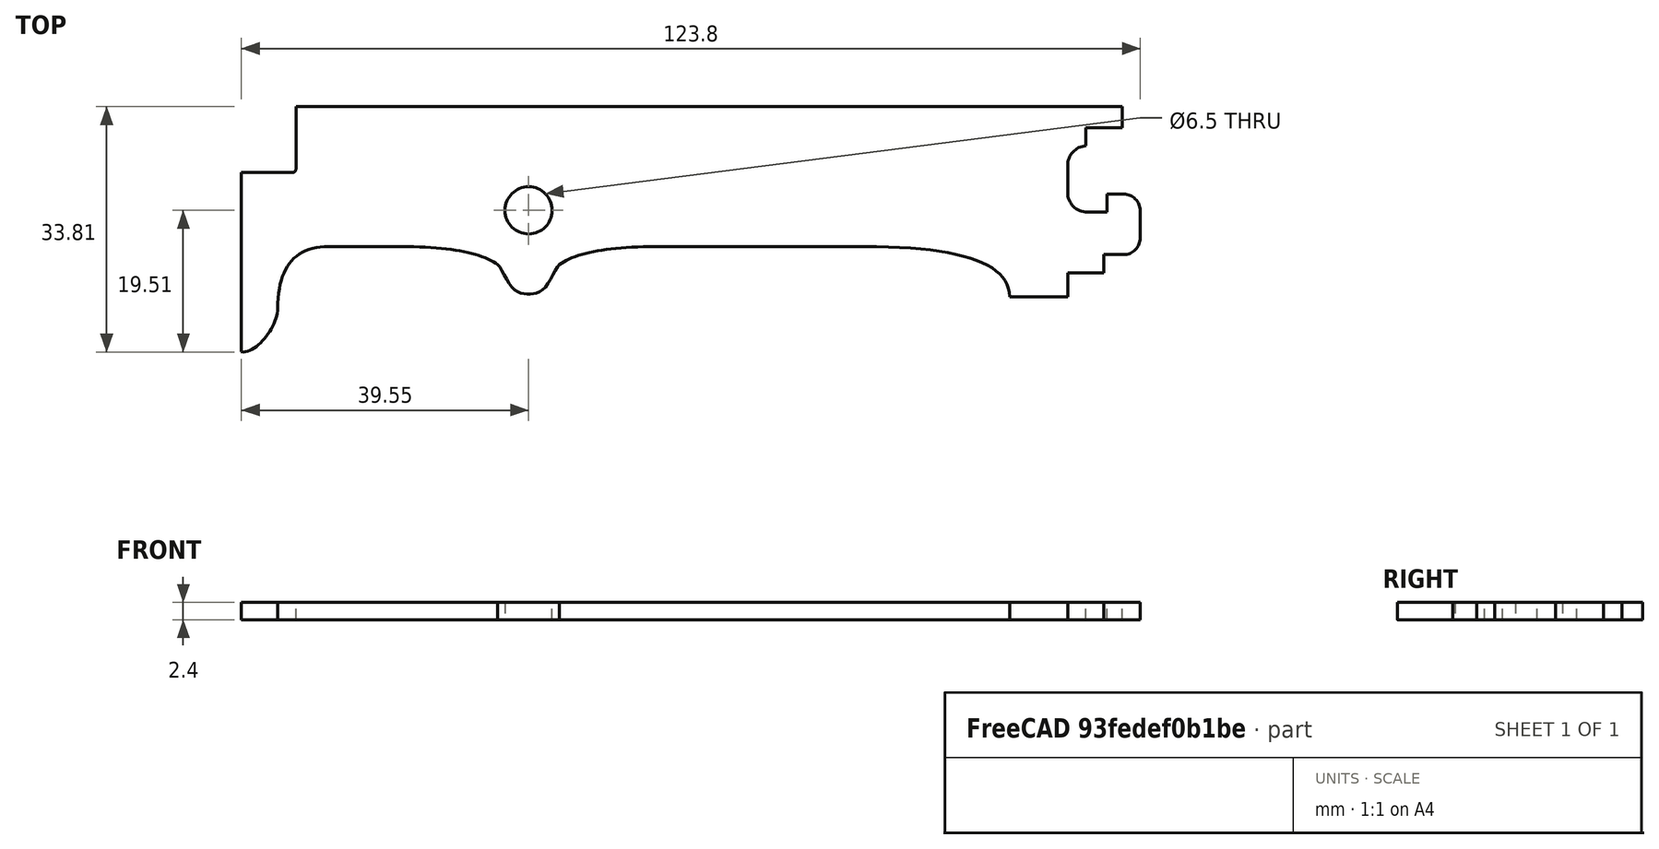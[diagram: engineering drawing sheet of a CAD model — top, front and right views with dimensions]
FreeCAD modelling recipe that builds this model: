
FCSTD DOCUMENT  (FreeCAD 0.19R0.19.2)
Label: v0_11
License: All rights reserved
LicenseURL: http://en.wikipedia.org/wiki/All_rights_reserved
objects: Sketcher::SketchObject×2, Part::Extrusion×1
note: 3 computed .brp shape members not serialized (recipe doc carries the construction recipe); baked Part::Feature solids carry a one-line shape summary decoded from their .brp

FEATURE [Sketcher::SketchObject] Sketch
  FullyConstrained = true
  sketch-geometry (69):
    g0: ArcOfCircle CenterX=-20 CenterY=-14.35 CenterZ=0 NormalX=0 NormalY=0 NormalZ=1 AngleXU=0 Radius=2.3 StartAngle=8e-16 EndAngle=1.5708
    g1: ArcOfCircle CenterX=-20 CenterY=-18.1 CenterZ=0 NormalX=0 NormalY=0 NormalZ=1 AngleXU=0 Radius=2.3 StartAngle=4.71239 EndAngle=6.28319
    g2: LineSegment StartX=-20 StartY=-20.4 StartZ=0 EndX=-22.7 EndY=-20.4 EndZ=0
    g3: LineSegment StartX=-22.7 StartY=-22.9 StartZ=0 EndX=-22.7 EndY=-20.4 EndZ=0
    g4: LineSegment StartX=-17.7 StartY=-14.35 StartZ=0 EndX=-17.7 EndY=-18.1 EndZ=0
    g5: LineSegment StartX=-25.2 StartY=-5.40742 StartZ=0 EndX=-25.2 EndY=-2.9 EndZ=0
    g6: LineSegment StartX=-25.2 StartY=-2.9 StartZ=0 EndX=-20.2 EndY=-2.9 EndZ=0
    g7: LineSegment StartX=-20.2 StartY=-2.9 StartZ=0 EndX=-20.2 EndY=0 EndZ=0
    g8: ArcOfCircle CenterX=-25 CenterY=-8.1 CenterZ=0 NormalX=0 NormalY=0 NormalZ=1 AngleXU=0 Radius=2.7 StartAngle=1.64494 EndAngle=3.14159
    g9: ArcOfCircle CenterX=-25 CenterY=-11.85 CenterZ=0 NormalX=0 NormalY=0 NormalZ=1 AngleXU=0 Radius=2.7 StartAngle=3.14159 EndAngle=4.71239
    g10: LineSegment StartX=-27.7 StartY=-8.1 StartZ=0 EndX=-27.7 EndY=-11.85 EndZ=0
    g11: LineSegment StartX=-25 StartY=-14.55 StartZ=0 EndX=-22.3 EndY=-14.55 EndZ=0
    g12: LineSegment StartX=-22.3 StartY=-12.05 StartZ=0 EndX=-22.3 EndY=-14.55 EndZ=0
    g13: LineSegment StartX=-22.3 StartY=-12.05 StartZ=0 EndX=-20 EndY=-12.05 EndZ=0
    g14: LineSegment StartX=-27.7 StartY=-22.9 StartZ=0 EndX=-22.7 EndY=-22.9 EndZ=0
    g15: LineSegment StartX=-27.7 StartY=-22.9 StartZ=0 EndX=-27.7 EndY=-26.2 EndZ=0
    g16: Circle CenterX=-101.95 CenterY=-14.3 CenterZ=0 NormalX=0 NormalY=0 NormalZ=1 AngleXU=0 Radius=3.25
    g17: LineSegment StartX=-134 StartY=0 StartZ=0 EndX=-20.2 EndY=0 EndZ=0
    g18: LineSegment StartX=-134 StartY=2.68e-14 StartZ=0 EndX=-134 EndY=-8.6 EndZ=0
    g19: LineSegment StartX=-134.5 StartY=-9.1 StartZ=0 EndX=-141.5 EndY=-9.1 EndZ=0
    g20: ArcOfCircle CenterX=-134.5 CenterY=-8.6 CenterZ=0 NormalX=0 NormalY=0 NormalZ=1 AngleXU=0 Radius=0.5 StartAngle=4.71239 EndAngle=6.28319
    g21: Circle CenterX=-97.7 CenterY=-21.8 CenterZ=0 NormalX=0 NormalY=0 NormalZ=1 AngleXU=0 Radius=1
    g22: Circle CenterX=-94.45 CenterY=-19.3 CenterZ=0 NormalX=0 NormalY=0 NormalZ=1 AngleXU=0 Radius=1
    g23: Circle CenterX=-84.45 CenterY=-19.3 CenterZ=0 NormalX=0 NormalY=0 NormalZ=1 AngleXU=0 Radius=1
    g24: BSplineCurve PolesCount=3 KnotsCount=2 Degree=2 IsPeriodic=0
    g25: GeomPoint X=-97.7 Y=-21.8 Z=0
    g26: GeomPoint X=-84.45 Y=-19.3 Z=0
    g27: Circle CenterX=-106.2 CenterY=-21.8 CenterZ=0 NormalX=0 NormalY=0 NormalZ=1 AngleXU=0 Radius=1
    g28: Circle CenterX=-109.45 CenterY=-19.3 CenterZ=0 NormalX=0 NormalY=0 NormalZ=1 AngleXU=0 Radius=1
    g29: Circle CenterX=-119.45 CenterY=-19.3 CenterZ=0 NormalX=0 NormalY=0 NormalZ=1 AngleXU=0 Radius=1
    g30: BSplineCurve PolesCount=3 KnotsCount=2 Degree=2 IsPeriodic=0
    g31: GeomPoint X=-106.2 Y=-21.8 Z=0
    g32: GeomPoint X=-119.45 Y=-19.3 Z=0
    g33: LineSegment StartX=-141.5 StartY=-9.1 StartZ=0 EndX=-141.5 EndY=-33.8 EndZ=0
    g34-g37: Circle x4 (B-spline internal-alignment scaffolding for g38; pole/knot coordinates omitted)
    g38: BSplineCurve PolesCount=4 KnotsCount=2 Degree=3 IsPeriodic=0
    g39: GeomPoint X=-141.5 Y=-33.8 Z=0
    g40: GeomPoint X=-136.5 Y=-27.8 Z=0
    g41: Circle CenterX=-136.5 CenterY=-27.8 CenterZ=0 NormalX=0 NormalY=0 NormalZ=1 AngleXU=0 Radius=1
    g42: Circle CenterX=-136.5 CenterY=-19.3 CenterZ=0 NormalX=0 NormalY=0 NormalZ=1 AngleXU=0 Radius=1
    g43: Circle CenterX=-129.5 CenterY=-19.3 CenterZ=0 NormalX=0 NormalY=0 NormalZ=1 AngleXU=0 Radius=1
    g44: BSplineCurve PolesCount=3 KnotsCount=2 Degree=2 IsPeriodic=0
    g45: GeomPoint X=-136.5 Y=-27.8 Z=0
    g46: GeomPoint X=-129.5 Y=-19.3 Z=0
    g47: LineSegment StartX=-129.5 StartY=-19.3 StartZ=0 EndX=-119.45 EndY=-19.3 EndZ=0
    g48: LineSegment StartX=-35.7 StartY=-26.2 StartZ=0 EndX=-27.7 EndY=-26.2 EndZ=0
    g49: Circle CenterX=-35.7 CenterY=-26.2 CenterZ=0 NormalX=0 NormalY=0 NormalZ=1 AngleXU=0 Radius=1
    g50: Circle CenterX=-35.7 CenterY=-19.3 CenterZ=0 NormalX=0 NormalY=0 NormalZ=1 AngleXU=0 Radius=1
    g51: Circle CenterX=-55.7 CenterY=-19.3 CenterZ=0 NormalX=0 NormalY=0 NormalZ=1 AngleXU=0 Radius=1
    g52: BSplineCurve PolesCount=3 KnotsCount=2 Degree=2 IsPeriodic=0
    g53: GeomPoint X=-35.7 Y=-26.2 Z=0
    g54: GeomPoint X=-55.7 Y=-19.3 Z=0
    g55: LineSegment StartX=-84.45 StartY=-19.3 StartZ=0 EndX=-55.7 EndY=-19.3 EndZ=0
    g56-g62: Circle x7 (B-spline internal-alignment scaffolding for g63; pole/knot coordinates omitted)
    g63: BSplineCurve PolesCount=7 KnotsCount=5 Degree=3 IsPeriodic=0
    g64-g68: GeomPoint x5 (B-spline internal-alignment scaffolding for g63; pole/knot coordinates omitted)
  constraints (111):
    c: Block(g1)
    c: Block(g0)
    c: Coincident(g2,g1)
    c: Horizontal(g2)
    c: Vertical(g3)
    c: Coincident(g3,g2)
    c: Coincident(g4,g0)
    c: Coincident(g4,g1)
    c: Vertical(g4)
    c: Vertical(g5)
    c: Block(g5)
    c: Coincident(g6,g5)
    c: Horizontal(g6)
    c: Vertical(g7)
    c: Block(g7)
    c: Block(g6)
    c: Coincident(g8,g5)
    c: Block(g9)
    c: Coincident(g10,g8)
    c: Coincident(g10,g9)
    c: Vertical(g10)
    c: Block(g10)
    c: Coincident(g11,g9)
    c: Horizontal(g11)
    c: Vertical(g12)
    c: Coincident(g12,g11)
    c: Block(g12)
    c: Coincident(g13,g0)
    c: Horizontal(g13)
    c: Block(g13)
    c: Coincident(g14,g3)
    c: Horizontal(g14)
    c: Block(g14)
    c: Coincident(g15,g14)
    c: Vertical(g15)
    c: Block(g16)
    c: Coincident(g17,g7)
    c: Horizontal(g17)
    c: Vertical(g18)
    c: Distance(g18) = 8.6
    c: Horizontal(g19)
    c: Distance(g19) = 7
    c: Coincident(g20,g18)
    c: Coincident(g20,g19)
    c: Block(g20)
    c: Block(g17)
    c: Weight(g21) = 1
    c: Equal(g21,g22)
    c: Equal(g21,g23)
    c: InternalAlignment(g21,g24)
    c: InternalAlignment(g22,g24)
    c: InternalAlignment(g23,g24)
    c: InternalAlignment(g25,g24)
    c: InternalAlignment(g26,g24)
    c: Weight(g27) = 1
    c: Equal(g27,g28)
    c: Equal(g27,g29)
    c: InternalAlignment(g27,g30)
    c: InternalAlignment(g28,g30)
    c: InternalAlignment(g29,g30)
    c: InternalAlignment(g31,g30)
    c: InternalAlignment(g32,g30)
    c: Block(g30)
    c: Block(g24)
    c: Coincident(g33,g19)
    c: Vertical(g33)
    c: Block(g33)
    c: Coincident(g38,g33)
    c: Weight(g34) = 1
    c: Equal(g34,g35)
    c: Equal(g34,g36)
    c: Equal(g34,g37)
    c: InternalAlignment(g34-g37 -> g38) x4
    c: InternalAlignment(g39,g38)
    c: InternalAlignment(g40,g38)
    c: Weight(g41) = 1
    c: Equal(g41,g42)
    c: Equal(g41,g43)
    c: InternalAlignment(g41,g44)
    c: InternalAlignment(g42,g44)
    c: InternalAlignment(g43,g44)
    c: InternalAlignment(g45,g44)
    c: InternalAlignment(g46,g44)
    c: Block(g38)
    c: Block(g44)
    c: Coincident(g47,g44)
    c: Coincident(g47,g30)
    c: Horizontal(g47)
    c: Horizontal(g48)
    c: Distance(g48) = 8
    c: Block(g48)
    c: Block(g15)
    c: Block(g8)
    c: Coincident(g52,g48)
    c: Weight(g49) = 1
    c: Equal(g49,g50)
    c: Equal(g49,g51)
    c: InternalAlignment(g49,g52)
    c: InternalAlignment(g50,g52)
    c: InternalAlignment(g51,g52)
    c: InternalAlignment(g53,g52)
    c: InternalAlignment(g54,g52)
    c: Block(g52)
    c: Coincident(g55,g24)
    c: Coincident(g55,g52)
    c: Horizontal(g55)
    c: Weight(g56) = 1
    c: Equal(g56, g57-g62) x6
    c: InternalAlignment(g56-g62 -> g63) x7
    c: InternalAlignment(g64-g68 -> g63) x5
    c: Block(g63)
FEATURE [Part::Extrusion] Extrude
  Base = -> Sketch
  Dir = (0,0,1)
  DirMode = 2
  FaceMakerClass = Part::FaceMakerBullseye
  LengthFwd = 2.4
  LengthRev = 0
  Solid = true
  Symmetric = false
FEATURE [Sketcher::SketchObject] Sketch001
  FullyConstrained = true
  sketch-geometry (69):
    g0: ArcOfCircle CenterX=-20 CenterY=-14.35 CenterZ=0 NormalX=0 NormalY=0 NormalZ=1 AngleXU=0 Radius=2.3 StartAngle=8e-16 EndAngle=1.5708
    g1: ArcOfCircle CenterX=-20 CenterY=-18.1 CenterZ=0 NormalX=0 NormalY=0 NormalZ=1 AngleXU=0 Radius=2.3 StartAngle=4.71239 EndAngle=6.28319
    g2: LineSegment StartX=-20 StartY=-20.4 StartZ=0 EndX=-22.7 EndY=-20.4 EndZ=0
    g3: LineSegment StartX=-22.7 StartY=-22.9 StartZ=0 EndX=-22.7 EndY=-20.4 EndZ=0
    g4: LineSegment StartX=-17.7 StartY=-14.35 StartZ=0 EndX=-17.7 EndY=-18.1 EndZ=0
    g5: LineSegment StartX=-25.2 StartY=-5.40742 StartZ=0 EndX=-25.2 EndY=-2.9 EndZ=0
    g6: LineSegment StartX=-25.2 StartY=-2.9 StartZ=0 EndX=-20.2 EndY=-2.9 EndZ=0
    g7: LineSegment StartX=-20.2 StartY=-2.9 StartZ=0 EndX=-20.2 EndY=0 EndZ=0
    g8: ArcOfCircle CenterX=-25 CenterY=-8.1 CenterZ=0 NormalX=0 NormalY=0 NormalZ=1 AngleXU=0 Radius=2.7 StartAngle=1.64494 EndAngle=3.14159
    g9: ArcOfCircle CenterX=-25 CenterY=-11.85 CenterZ=0 NormalX=0 NormalY=0 NormalZ=1 AngleXU=0 Radius=2.7 StartAngle=3.14159 EndAngle=4.71239
    g10: LineSegment StartX=-27.7 StartY=-8.1 StartZ=0 EndX=-27.7 EndY=-11.85 EndZ=0
    g11: LineSegment StartX=-25 StartY=-14.55 StartZ=0 EndX=-22.3 EndY=-14.55 EndZ=0
    g12: LineSegment StartX=-22.3 StartY=-12.05 StartZ=0 EndX=-22.3 EndY=-14.55 EndZ=0
    g13: LineSegment StartX=-22.3 StartY=-12.05 StartZ=0 EndX=-20 EndY=-12.05 EndZ=0
    g14: LineSegment StartX=-27.7 StartY=-22.9 StartZ=0 EndX=-22.7 EndY=-22.9 EndZ=0
    g15: LineSegment StartX=-27.7 StartY=-22.9 StartZ=0 EndX=-27.7 EndY=-26.2 EndZ=0
    g16: Circle CenterX=-101.95 CenterY=-14.3 CenterZ=0 NormalX=0 NormalY=0 NormalZ=1 AngleXU=0 Radius=3.25
    g17: LineSegment StartX=-134 StartY=0 StartZ=0 EndX=-20.2 EndY=0 EndZ=0
    g18: LineSegment StartX=-134 StartY=2.68e-14 StartZ=0 EndX=-134 EndY=-8.6 EndZ=0
    g19: LineSegment StartX=-134.5 StartY=-9.1 StartZ=0 EndX=-141.5 EndY=-9.1 EndZ=0
    g20: ArcOfCircle CenterX=-134.5 CenterY=-8.6 CenterZ=0 NormalX=0 NormalY=0 NormalZ=1 AngleXU=0 Radius=0.5 StartAngle=4.71239 EndAngle=6.28319
    g21: Circle CenterX=-97.7 CenterY=-21.8 CenterZ=0 NormalX=0 NormalY=0 NormalZ=1 AngleXU=0 Radius=1
    g22: Circle CenterX=-94.45 CenterY=-19.3 CenterZ=0 NormalX=0 NormalY=0 NormalZ=1 AngleXU=0 Radius=1
    g23: Circle CenterX=-84.45 CenterY=-19.3 CenterZ=0 NormalX=0 NormalY=0 NormalZ=1 AngleXU=0 Radius=1
    g24: BSplineCurve PolesCount=3 KnotsCount=2 Degree=2 IsPeriodic=0
    g25: GeomPoint X=-97.7 Y=-21.8 Z=0
    g26: GeomPoint X=-84.45 Y=-19.3 Z=0
    g27: Circle CenterX=-106.2 CenterY=-21.8 CenterZ=0 NormalX=0 NormalY=0 NormalZ=1 AngleXU=0 Radius=1
    g28: Circle CenterX=-109.45 CenterY=-19.3 CenterZ=0 NormalX=0 NormalY=0 NormalZ=1 AngleXU=0 Radius=1
    g29: Circle CenterX=-119.45 CenterY=-19.3 CenterZ=0 NormalX=0 NormalY=0 NormalZ=1 AngleXU=0 Radius=1
    g30: BSplineCurve PolesCount=3 KnotsCount=2 Degree=2 IsPeriodic=0
    g31: GeomPoint X=-106.2 Y=-21.8 Z=0
    g32: GeomPoint X=-119.45 Y=-19.3 Z=0
    g33: LineSegment StartX=-141.5 StartY=-9.1 StartZ=0 EndX=-141.5 EndY=-33.8 EndZ=0
    g34-g37: Circle x4 (B-spline internal-alignment scaffolding for g38; pole/knot coordinates omitted)
    g38: BSplineCurve PolesCount=4 KnotsCount=2 Degree=3 IsPeriodic=0
    g39: GeomPoint X=-141.5 Y=-33.8 Z=0
    g40: GeomPoint X=-136.5 Y=-27.8 Z=0
    g41: Circle CenterX=-136.5 CenterY=-27.8 CenterZ=0 NormalX=0 NormalY=0 NormalZ=1 AngleXU=0 Radius=1
    g42: Circle CenterX=-136.5 CenterY=-19.3 CenterZ=0 NormalX=0 NormalY=0 NormalZ=1 AngleXU=0 Radius=1
    g43: Circle CenterX=-129.5 CenterY=-19.3 CenterZ=0 NormalX=0 NormalY=0 NormalZ=1 AngleXU=0 Radius=1
    g44: BSplineCurve PolesCount=3 KnotsCount=2 Degree=2 IsPeriodic=0
    g45: GeomPoint X=-136.5 Y=-27.8 Z=0
    g46: GeomPoint X=-129.5 Y=-19.3 Z=0
    g47: LineSegment StartX=-129.5 StartY=-19.3 StartZ=0 EndX=-119.45 EndY=-19.3 EndZ=0
    g48: LineSegment StartX=-35.7 StartY=-26.2 StartZ=0 EndX=-27.7 EndY=-26.2 EndZ=0
    g49: Circle CenterX=-35.7 CenterY=-26.2 CenterZ=0 NormalX=0 NormalY=0 NormalZ=1 AngleXU=0 Radius=1
    g50: Circle CenterX=-35.7 CenterY=-19.3 CenterZ=0 NormalX=0 NormalY=0 NormalZ=1 AngleXU=0 Radius=1
    g51: Circle CenterX=-55.7 CenterY=-19.3 CenterZ=0 NormalX=0 NormalY=0 NormalZ=1 AngleXU=0 Radius=1
    g52: BSplineCurve PolesCount=3 KnotsCount=2 Degree=2 IsPeriodic=0
    g53: GeomPoint X=-35.7 Y=-26.2 Z=0
    g54: GeomPoint X=-55.7 Y=-19.3 Z=0
    g55: LineSegment StartX=-84.45 StartY=-19.3 StartZ=0 EndX=-55.7 EndY=-19.3 EndZ=0
    g56-g62: Circle x7 (B-spline internal-alignment scaffolding for g63; pole/knot coordinates omitted)
    g63: BSplineCurve PolesCount=7 KnotsCount=5 Degree=3 IsPeriodic=0
    g64-g68: GeomPoint x5 (B-spline internal-alignment scaffolding for g63; pole/knot coordinates omitted)
  constraints (111):
    c: Block(g1)
    c: Block(g0)
    c: Coincident(g2,g1)
    c: Horizontal(g2)
    c: Vertical(g3)
    c: Coincident(g3,g2)
    c: Coincident(g4,g0)
    c: Coincident(g4,g1)
    c: Vertical(g4)
    c: Vertical(g5)
    c: Block(g5)
    c: Coincident(g6,g5)
    c: Horizontal(g6)
    c: Vertical(g7)
    c: Block(g7)
    c: Block(g6)
    c: Coincident(g8,g5)
    c: Block(g9)
    c: Coincident(g10,g8)
    c: Coincident(g10,g9)
    c: Vertical(g10)
    c: Block(g10)
    c: Coincident(g11,g9)
    c: Horizontal(g11)
    c: Vertical(g12)
    c: Coincident(g12,g11)
    c: Block(g12)
    c: Coincident(g13,g0)
    c: Horizontal(g13)
    c: Block(g13)
    c: Coincident(g14,g3)
    c: Horizontal(g14)
    c: Block(g14)
    c: Coincident(g15,g14)
    c: Vertical(g15)
    c: Block(g16)
    c: Coincident(g17,g7)
    c: Horizontal(g17)
    c: Vertical(g18)
    c: Distance(g18) = 8.6
    c: Horizontal(g19)
    c: Distance(g19) = 7
    c: Coincident(g20,g18)
    c: Coincident(g20,g19)
    c: Block(g20)
    c: Block(g17)
    c: Weight(g21) = 1
    c: Equal(g21,g22)
    c: Equal(g21,g23)
    c: InternalAlignment(g21,g24)
    c: InternalAlignment(g22,g24)
    c: InternalAlignment(g23,g24)
    c: InternalAlignment(g25,g24)
    c: InternalAlignment(g26,g24)
    c: Weight(g27) = 1
    c: Equal(g27,g28)
    c: Equal(g27,g29)
    c: InternalAlignment(g27,g30)
    c: InternalAlignment(g28,g30)
    c: InternalAlignment(g29,g30)
    c: InternalAlignment(g31,g30)
    c: InternalAlignment(g32,g30)
    c: Block(g30)
    c: Block(g24)
    c: Coincident(g33,g19)
    c: Vertical(g33)
    c: Block(g33)
    c: Coincident(g38,g33)
    c: Weight(g34) = 1
    c: Equal(g34,g35)
    c: Equal(g34,g36)
    c: Equal(g34,g37)
    c: InternalAlignment(g34-g37 -> g38) x4
    c: InternalAlignment(g39,g38)
    c: InternalAlignment(g40,g38)
    c: Weight(g41) = 1
    c: Equal(g41,g42)
    c: Equal(g41,g43)
    c: InternalAlignment(g41,g44)
    c: InternalAlignment(g42,g44)
    c: InternalAlignment(g43,g44)
    c: InternalAlignment(g45,g44)
    c: InternalAlignment(g46,g44)
    c: Block(g38)
    c: Block(g44)
    c: Coincident(g47,g44)
    c: Coincident(g47,g30)
    c: Horizontal(g47)
    c: Horizontal(g48)
    c: Distance(g48) = 8
    c: Block(g48)
    c: Block(g15)
    c: Block(g8)
    c: Coincident(g52,g48)
    c: Weight(g49) = 1
    c: Equal(g49,g50)
    c: Equal(g49,g51)
    c: InternalAlignment(g49,g52)
    c: InternalAlignment(g50,g52)
    c: InternalAlignment(g51,g52)
    c: InternalAlignment(g53,g52)
    c: InternalAlignment(g54,g52)
    c: Block(g52)
    c: Coincident(g55,g24)
    c: Coincident(g55,g52)
    c: Horizontal(g55)
    c: Weight(g56) = 1
    c: Equal(g56, g57-g62) x6
    c: InternalAlignment(g56-g62 -> g63) x7
    c: InternalAlignment(g64-g68 -> g63) x5
    c: Block(g63)
